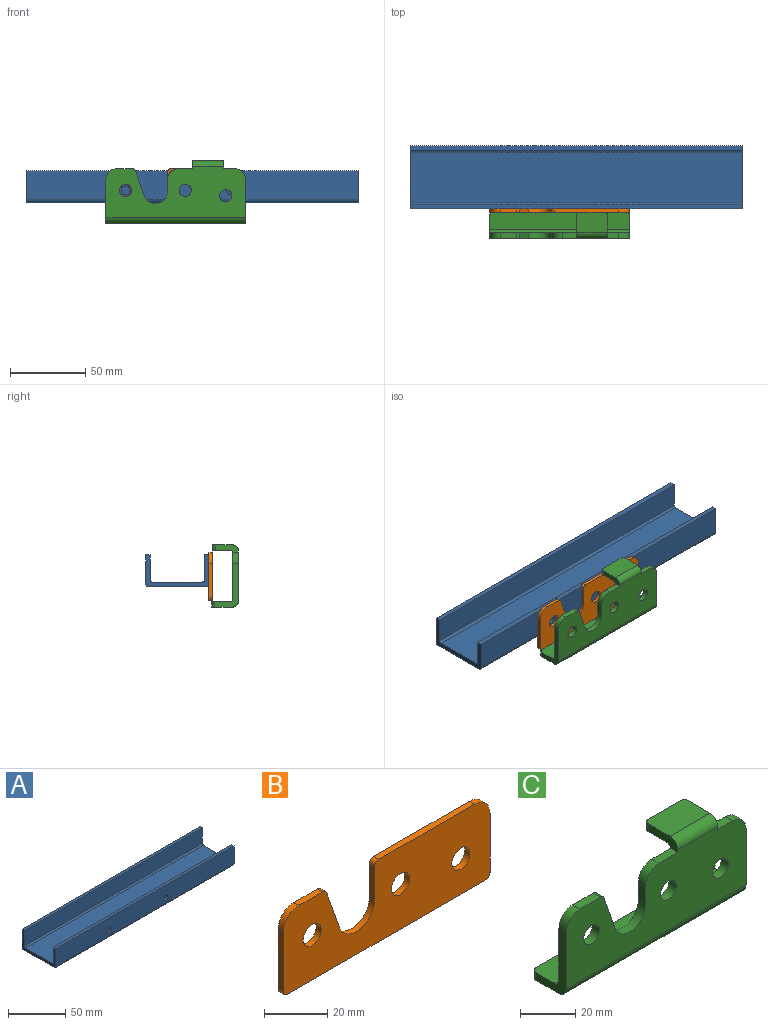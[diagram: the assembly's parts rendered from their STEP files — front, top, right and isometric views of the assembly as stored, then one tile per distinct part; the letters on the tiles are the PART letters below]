
ASSEMBLY  parts=3 mates=1
PART A: 16 faces, bbox 220x42x21 mm
  f0: plane 220x33mm, normal (0,0,1), area 7260mm2, adj f8,f9,f12,f13
  f1: plane 220x16.5mm, normal (0,1,0), area 3573.5mm2, adj f2,f8,f9,f12,f14,f15
  f2: plane 220x3mm, normal (0,0,1), area 660mm2, adj f1,f3,f8,f9
  f3: plane 220x19mm, normal (0,-1,0), area 4123.5mm2, adj f2,f8,f9,f10,f14,f15
  f4: plane 220x38mm, normal (0,0,-1), area 8360mm2, adj f8,f9,f10,f11
  f5: plane 220x19mm, normal (0,1,0), area 4180mm2, adj f6,f8,f9,f11
  f6: plane 220x3mm, normal (0,0,1), area 660mm2, adj f5,f7,f8,f9
  f7: plane 220x16.5mm, normal (0,-1,0), area 3630mm2, adj f6,f8,f9,f13
  f8: plane 42x21mm, normal (-1,0,0), area 233.2mm2, adj f0,f1,f2,f3,f4,f5,f6,f7
  f9: plane 42x21mm, normal (1,0,0), area 233.2mm2, adj f0,f1,f2,f3,f4,f5,f6,f7
  f10: cylinder r=2mm len=220mm, axis (-1,0,0), area 691.2mm2, adj f3,f4,f8,f9
  f11: cylinder r=2mm len=220mm, axis (1,0,0), area 691.2mm2, adj f4,f5,f8,f9
  f12: cylinder r=1.5mm len=220mm, axis (1,0,0), area 518.4mm2, adj f0,f1,f8,f9
  f13: cylinder r=1.5mm len=220mm, axis (-1,0,0), area 518.4mm2, adj f0,f7,f8,f9
  f14: cylinder r=3mm len=6mm, axis (0,-1,0), area 56.5mm2, adj f1,f3
  f15: cylinder r=3mm len=6mm, axis (0,-1,0), area 56.5mm2, adj f1,f3
PART B: 19 faces, bbox 92.4x2.3x31.8 mm
  f0: cylinder r=4.05mm len=8.1mm, axis (0,-1,0), area 58.5mm2, adj f13,f14
  f1: cylinder r=4.05mm len=8.1mm, axis (0,-1,0), area 58.5mm2, adj f13,f14
  f2: cylinder r=4.05mm len=8.1mm, axis (0,-1,0), area 58.5mm2, adj f13,f14
  f3: cylinder r=7mm len=7mm, axis (0,1,0), area 25.3mm2, adj f4,f13,f14,f15
  f4: plane 10.58x2.3mm, normal (0,0,1), area 24.3mm2, adj f3,f5,f13,f14
  f5: cylinder r=2mm len=2.3mm, axis (0,1,0), area 5.7mm2, adj f4,f6,f13,f14
  f6: plane 16.32x5.73mm, normal (0.94,0,0.33), area 39.8mm2, adj f5,f7,f13,f14
  f7: cylinder r=8mm len=15.55mm, axis (0,-1,0), area 51.6mm2, adj f6,f8,f13,f14
  f8: plane 13x2.3mm, normal (-1,0,0), area 29.9mm2, adj f7,f9,f13,f14
  f9: cylinder r=2mm len=2.3mm, axis (0,-1,0), area 7.2mm2, adj f8,f10,f13,f14
  f10: plane 42.65x2.3mm, normal (0,0,1), area 98.1mm2, adj f9,f11,f13,f14
  f11: cylinder r=7mm len=7mm, axis (0,-1,0), area 25.3mm2, adj f10,f12,f13,f14
  f12: plane 22.8x2.3mm, normal (1,0,0), area 52.4mm2, adj f11,f13,f14,f17
  f13: plane 92.4x31.8mm, normal (0,-1,0), area 2372.1mm2, adj f0,f1,f2,f3,f4,f5,f6,f7
  f14: plane 92.4x31.8mm, normal (0,1,0), area 2372.1mm2, adj f0,f1,f2,f3,f4,f5,f6,f7
  f15: plane 22.8x2.3mm, normal (-1,0,0), area 52.4mm2, adj f3,f13,f14,f18
  f16: plane 88.4x2.3mm, normal (0,0,-1), area 203.3mm2, adj f13,f14,f17,f18
  f17: cylinder r=2mm len=2.3mm, axis (0,1,0), area 7.2mm2, adj f12,f13,f14,f16
  f18: cylinder r=2mm len=2.3mm, axis (0,-1,0), area 7.2mm2, adj f13,f14,f15,f16
PART C: 33 faces, bbox 92.4x17.7x41.2 mm
  f0: plane 29x15.7mm, normal (-1,0,0), area 146.7mm2, adj f5,f15,f16,f19,f21,f25,f30,f31
  f1: plane 29x15.7mm, normal (1,0,0), area 146.7mm2, adj f5,f15,f16,f19,f21,f26,f29,f31
  f2: cylinder r=8mm len=15.55mm, axis (0,-1,0), area 83mm2, adj f3,f14,f15,f19
  f3: plane 16.32x5.73mm, normal (0.94,0,0.33), area 64mm2, adj f2,f15,f19,f22
  f4: plane 10.58x3.7mm, normal (0,0,1), area 39.2mm2, adj f15,f19,f22,f25
  f5: plane 92.4x13.7mm, normal (0,0,-1), area 1264.2mm2, adj f0,f1,f21,f28,f29,f30
  f6: plane 7.5x3.72mm, normal (0,0,1), area 27.9mm2, adj f7,f15,f26,f32
  f7: plane 15.2x5.2mm, normal (1,0,0), area 56.9mm2, adj f6,f8,f15,f17,f20,f23,f32
  f8: plane 20.5x13.2mm, normal (0,0,1), area 268.9mm2, adj f7,f9,f18,f20,f23,f24
  f9: plane 15.2x5.2mm, normal (-1,0,0), area 56.9mm2, adj f8,f10,f15,f17,f20,f24,f32
  f10: plane 9.65x3.72mm, normal (0,0,1), area 35.9mm2, adj f9,f15,f27,f32
  f11: cylinder r=4.05mm len=8.1mm, axis (0,-1,0), area 94.2mm2, adj f15,f19
  f12: cylinder r=4.05mm len=8.1mm, axis (0,-1,0), area 94.2mm2, adj f15,f19
  f13: cylinder r=4.05mm len=8.1mm, axis (0,-1,0), area 94.2mm2, adj f15,f19
  f14: plane 8x3.7mm, normal (-1,0,0), area 29.6mm2, adj f2,f15,f19,f27
  f15: plane 92.4x33.2mm, normal (0,-1,0), area 2407.2mm2, adj f0,f1,f2,f3,f4,f6,f7,f9
  f16: plane 92.4x12mm, normal (0,0,1), area 1107.1mm2, adj f0,f1,f28,f29,f30,f31
  f17: plane 20.5x11.5mm, normal (0,0,-1), area 234mm2, adj f7,f9,f18,f23,f24,f32
  f18: plane 16.5x3.5mm, normal (0,1,0), area 57.8mm2, adj f8,f17,f23,f24
  f19: plane 92.4x30.5mm, normal (0,1,0), area 2231.9mm2, adj f0,f1,f2,f3,f4,f11,f12,f13
  f20: cylinder r=4mm len=20.5mm, axis (-1,0,0), area 128.8mm2, adj f7,f8,f9,f15
  f21: cylinder r=4mm len=92.4mm, axis (1,0,0), area 580.6mm2, adj f0,f1,f5,f15
  f22: cylinder r=2mm len=3.7mm, axis (0,1,0), area 9.1mm2, adj f3,f4,f15,f19
  f23: cylinder r=2mm len=3.5mm, axis (0,0,1), area 11mm2, adj f7,f8,f17,f18
  f24: cylinder r=2mm len=3.5mm, axis (0,0,-1), area 11mm2, adj f8,f9,f17,f18
  f25: cylinder r=7mm len=7mm, axis (0,1,0), area 40.7mm2, adj f0,f4,f15,f19
  f26: cylinder r=7mm len=7mm, axis (0,-1,0), area 40.7mm2, adj f1,f6,f15,f19,f32
  f27: cylinder r=7mm len=7mm, axis (0,-1,0), area 40.7mm2, adj f10,f14,f15,f19,f32
  f28: plane 88.4x3.5mm, normal (0,1,0), area 309.4mm2, adj f5,f16,f29,f30
  f29: cylinder r=2mm len=3.5mm, axis (0,0,1), area 11mm2, adj f1,f5,f16,f28
  f30: cylinder r=2mm len=3.5mm, axis (0,0,-1), area 11mm2, adj f0,f5,f16,f28
  f31: cylinder r=2mm len=92.4mm, axis (1,0,0), area 290.3mm2, adj f0,f1,f16,f19
  f32: cylinder r=2mm len=41.7mm, axis (-1,0,0), area 70.4mm2, adj f6,f7,f9,f10,f17,f19,f26,f27
PLACE A t=(118.24,8.19,-4.46)mm fixed
PLACE B t=(-17.76,-32.31,2.94)mm
PLACE C t=(-17.76,-32.31,2.94)mm
MATE fastened B.f1 <-> A.f15  axis (0,1,0) through (-35.76,-12.81,3.54)mm
